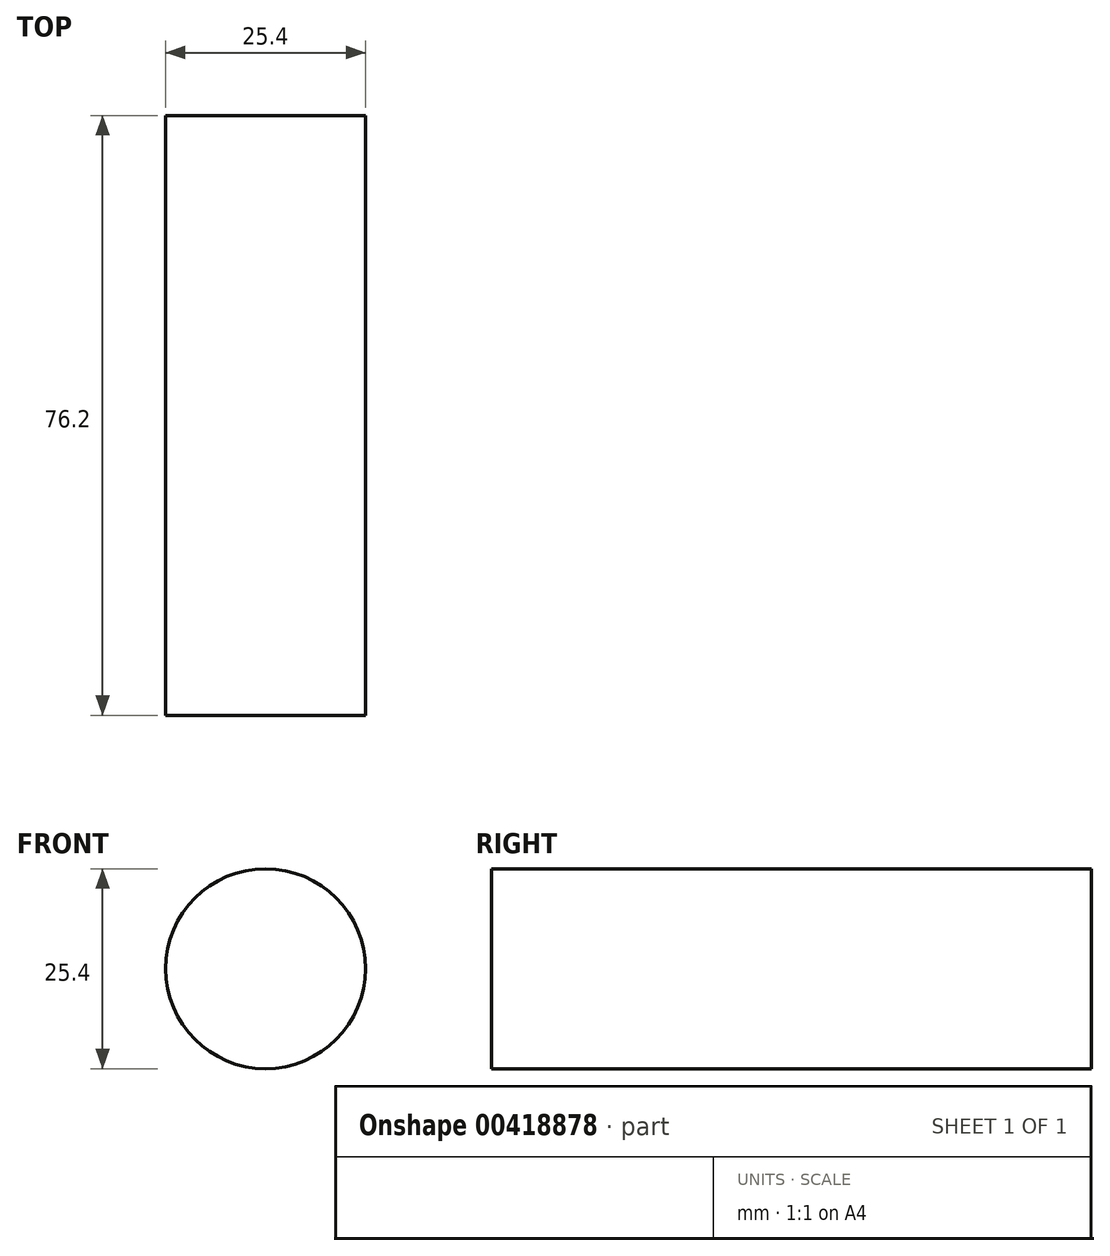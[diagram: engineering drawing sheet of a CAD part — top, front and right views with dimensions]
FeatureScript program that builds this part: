
annotation { "Feature Type Name" : "Feature", "Feature Type Description" : "" }
export const myFeature = defineFeature(function(context is Context, id is Id, definition is map)
    precondition{}
    {
        {
            var Q0;
            Q0=qCreatedBy(makeId("Front.planeOp"),FACE);
            var sketch = newSketch(context, id + "F0", { "sketchPlane" : qUnion([Q0])});
            skCircle(sketch, "E0", {"center": v(-12.6, 13.56) * mm, "radius": 12.7 * mm});
            skSolve(sketch);
        }
        {
            var Q0;
            Q0 = qSketchRegion(id + "F0", true);
            extrude(context, id + "F1", {"entities" : qUnion([Q0]), "depth" : 76.2 * mm});
        }
    });
